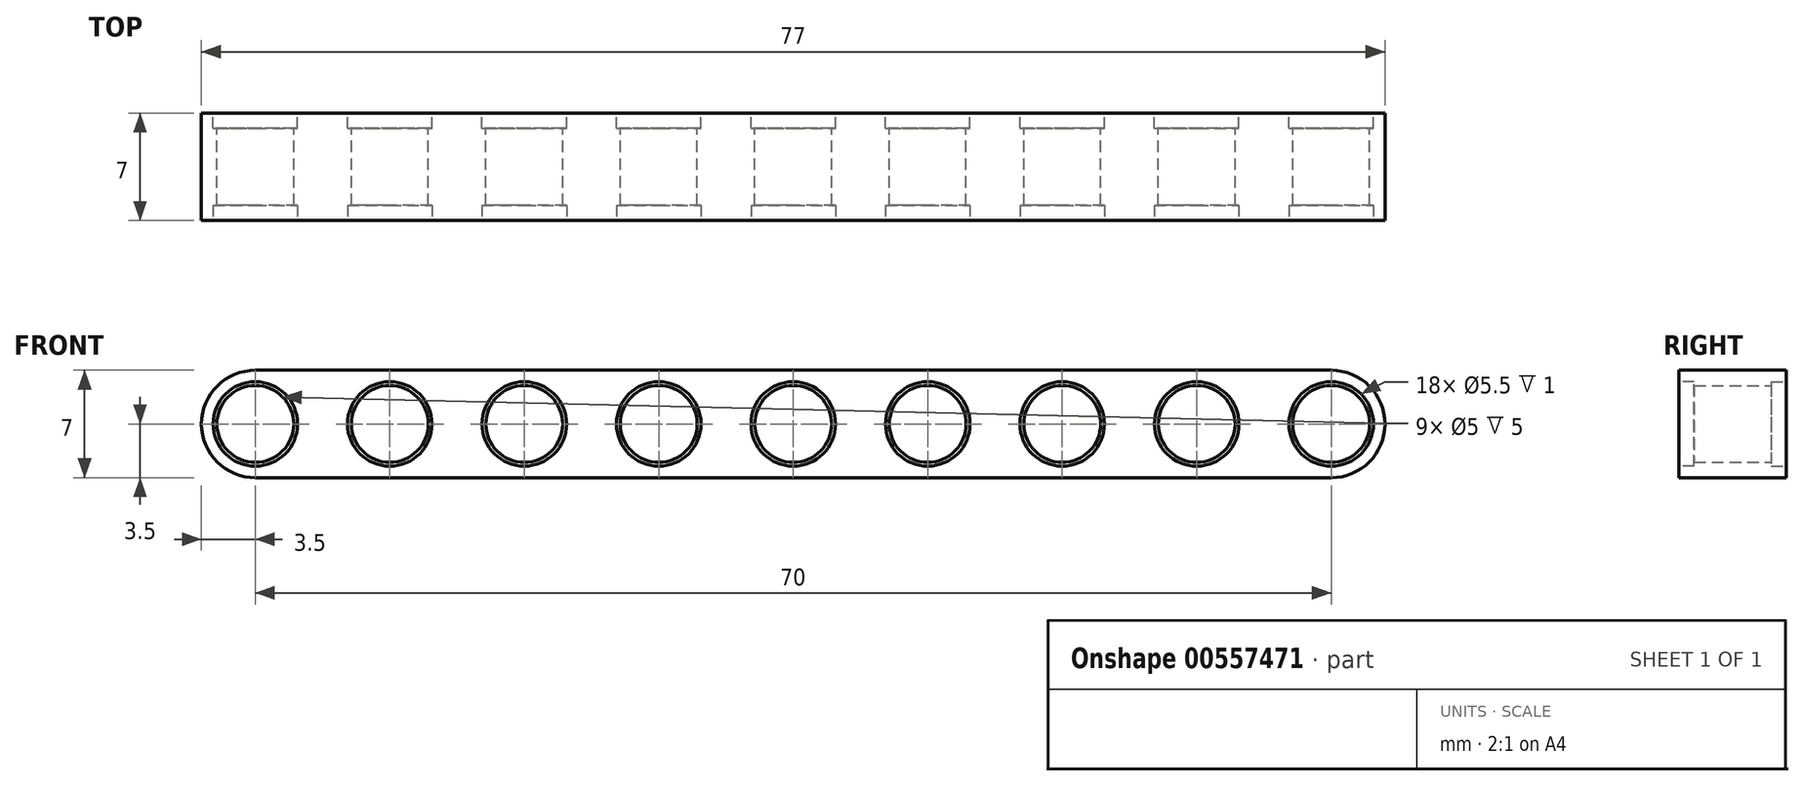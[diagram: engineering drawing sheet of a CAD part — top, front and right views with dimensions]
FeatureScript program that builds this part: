
annotation { "Feature Type Name" : "Feature", "Feature Type Description" : "" }
export const myFeature = defineFeature(function(context is Context, id is Id, definition is map)
    precondition{}
    {
        {
            var Q0;
            Q0=qCreatedBy(makeId("Front.planeOp"),FACE);
            var sketch = newSketch(context, id + "F0", { "sketchPlane" : qUnion([Q0])});
            skLineSegment(sketch, "E0.bottom", {"start": v(35, 3.5) * mm, "end": v(-35, 3.5) * mm});
            skLineSegment(sketch, "E0.top", {"start": v(35, -3.5) * mm, "end": v(-35, -3.5) * mm});
            skPoint(sketch, "E0.middle", {"position": v(0, 0) * mm});
            skArc(sketch, "E1", {"start": v(-35, 3.5) * mm, "mid": v(-38.5, 0) * mm, "end": v(-35, -3.5) * mm});
            skArc(sketch, "E2", {"start": v(35, -3.5) * mm, "mid": v(38.5, 0) * mm, "end": v(35, 3.5) * mm});
            skCircle(sketch, "E3", {"center": v(-35, 0) * mm, "radius": 2.5 * mm});
            skCircle(sketch, "E4.1.0.0", {"center": v(-26.25, 0) * mm, "radius": 2.5 * mm});
            skCircle(sketch, "E4.2.0.0", {"center": v(-17.5, 0) * mm, "radius": 2.5 * mm});
            skCircle(sketch, "E4.3.0.0", {"center": v(-8.75, 0) * mm, "radius": 2.5 * mm});
            skCircle(sketch, "E4.4.0.0", {"center": v(0, 0) * mm, "radius": 2.5 * mm});
            skCircle(sketch, "E4.5.0.0", {"center": v(8.75, 0) * mm, "radius": 2.5 * mm});
            skCircle(sketch, "E4.6.0.0", {"center": v(17.5, 0) * mm, "radius": 2.5 * mm});
            skCircle(sketch, "E4.7.0.0", {"center": v(26.25, 0) * mm, "radius": 2.5 * mm});
            skCircle(sketch, "E4.8.0.0", {"center": v(35, 0) * mm, "radius": 2.5 * mm});
            skLineSegment(sketch, "E4.direction1", {"start": v(-35, 0) * mm, "end": v(-26.25, 0) * mm, "construction": true});
            skSolve(sketch);
        }
        {
            var Q0;
            Q0=makeQuery(id+"F0.imprint","IMPRINT",FACE,{"disambiguationData":[TD([[makeQuery(id+"F0.imprint","IMPRINT",EDGE,{"derivedFrom":sQuery(id+"F0.wireOp",EDGE,"E0.bottom")}),1.0]])]});
            extrude(context, id + "F1", {"entities" : qUnion([Q0]), "depth" : 7 * mm, "offsetDistance" : 25 * mm});
        }
        {
            var Q0;
            Q0=makeQuery(id+"F1.opExtrude","CAP_FACE",FACE,{"disambiguationData":[OSD([sQuery(id+"F0.wireOp",EDGE,"E0.bottom"),sQuery(id+"F0.wireOp",EDGE,"E0.top"),sQuery(id+"F0.wireOp",EDGE,"E1"),sQuery(id+"F0.wireOp",EDGE,"E2"),sQuery(id+"F0.wireOp",EDGE,"E3"),sQuery(id+"F0.wireOp",EDGE,"E4.1.0.0"),sQuery(id+"F0.wireOp",EDGE,"E4.2.0.0"),sQuery(id+"F0.wireOp",EDGE,"E4.3.0.0"),sQuery(id+"F0.wireOp",EDGE,"E4.4.0.0"),sQuery(id+"F0.wireOp",EDGE,"E4.5.0.0"),sQuery(id+"F0.wireOp",EDGE,"E4.6.0.0"),sQuery(id+"F0.wireOp",EDGE,"E4.7.0.0"),sQuery(id+"F0.wireOp",EDGE,"E4.8.0.0")])],"isStart":false});
            var sketch = newSketch(context, id + "F2", { "sketchPlane" : qUnion([Q0])});
            skCircle(sketch, "E5", {"center": v(35, 0) * mm, "radius": 2.75 * mm});
            skCircle(sketch, "E6.1.0.0", {"center": v(26.25, 0) * mm, "radius": 2.75 * mm});
            skCircle(sketch, "E6.2.0.0", {"center": v(17.5, 0) * mm, "radius": 2.75 * mm});
            skCircle(sketch, "E6.3.0.0", {"center": v(8.75, 0) * mm, "radius": 2.75 * mm});
            skCircle(sketch, "E6.4.0.0", {"center": v(0, 0) * mm, "radius": 2.75 * mm});
            skCircle(sketch, "E6.5.0.0", {"center": v(-8.75, 0) * mm, "radius": 2.75 * mm});
            skCircle(sketch, "E6.6.0.0", {"center": v(-17.5, 0) * mm, "radius": 2.75 * mm});
            skCircle(sketch, "E6.7.0.0", {"center": v(-26.25, 0) * mm, "radius": 2.75 * mm});
            skCircle(sketch, "E6.8.0.0", {"center": v(-35, 0) * mm, "radius": 2.75 * mm});
            skLineSegment(sketch, "E6.direction1", {"start": v(35, 0) * mm, "end": v(26.25, 0) * mm, "construction": true});
            skSolve(sketch);
        }
        {
            var Q0;
            Q0 = qSketchRegion(id + "F2", true);
            extrude(context, id + "F3", {"entities" : qUnion([Q0]), "operationType" : NewBodyOperationType.REMOVE, "oppositeDirection" : true, "depth" : 1 * mm, "offsetDistance" : 25 * mm});
        }
        {
            var Q0;
            Q0=makeQuery(id+"F1.opExtrude","CAP_FACE",FACE,{"disambiguationData":[OSD([sQuery(id+"F0.wireOp",EDGE,"E0.bottom"),sQuery(id+"F0.wireOp",EDGE,"E0.top"),sQuery(id+"F0.wireOp",EDGE,"E1"),sQuery(id+"F0.wireOp",EDGE,"E2"),sQuery(id+"F0.wireOp",EDGE,"E3"),sQuery(id+"F0.wireOp",EDGE,"E4.1.0.0"),sQuery(id+"F0.wireOp",EDGE,"E4.2.0.0"),sQuery(id+"F0.wireOp",EDGE,"E4.3.0.0"),sQuery(id+"F0.wireOp",EDGE,"E4.4.0.0"),sQuery(id+"F0.wireOp",EDGE,"E4.5.0.0"),sQuery(id+"F0.wireOp",EDGE,"E4.6.0.0"),sQuery(id+"F0.wireOp",EDGE,"E4.7.0.0"),sQuery(id+"F0.wireOp",EDGE,"E4.8.0.0")])],"isStart":true});
            var sketch = newSketch(context, id + "F4", { "sketchPlane" : qUnion([Q0])});
            skCircle(sketch, "E7", {"center": v(-35, 0) * mm, "radius": 2.75 * mm});
            skCircle(sketch, "E8.1.0.0", {"center": v(-26.25, 0) * mm, "radius": 2.75 * mm});
            skCircle(sketch, "E8.2.0.0", {"center": v(-17.5, 0) * mm, "radius": 2.75 * mm});
            skCircle(sketch, "E8.3.0.0", {"center": v(-8.75, 0) * mm, "radius": 2.75 * mm});
            skCircle(sketch, "E8.4.0.0", {"center": v(0, 0) * mm, "radius": 2.75 * mm});
            skCircle(sketch, "E8.5.0.0", {"center": v(8.75, 0) * mm, "radius": 2.75 * mm});
            skCircle(sketch, "E8.6.0.0", {"center": v(17.5, 0) * mm, "radius": 2.75 * mm});
            skCircle(sketch, "E8.7.0.0", {"center": v(26.25, 0) * mm, "radius": 2.75 * mm});
            skCircle(sketch, "E8.8.0.0", {"center": v(35, 0) * mm, "radius": 2.75 * mm});
            skLineSegment(sketch, "E8.direction1", {"start": v(-35, 0) * mm, "end": v(-26.25, 0) * mm, "construction": true});
            skSolve(sketch);
        }
        {
            var Q0;
            Q0 = qSketchRegion(id + "F4", true);
            extrude(context, id + "F5", {"entities" : qUnion([Q0]), "operationType" : NewBodyOperationType.REMOVE, "oppositeDirection" : true, "depth" : 1 * mm, "offsetDistance" : 25 * mm});
        }
    });
